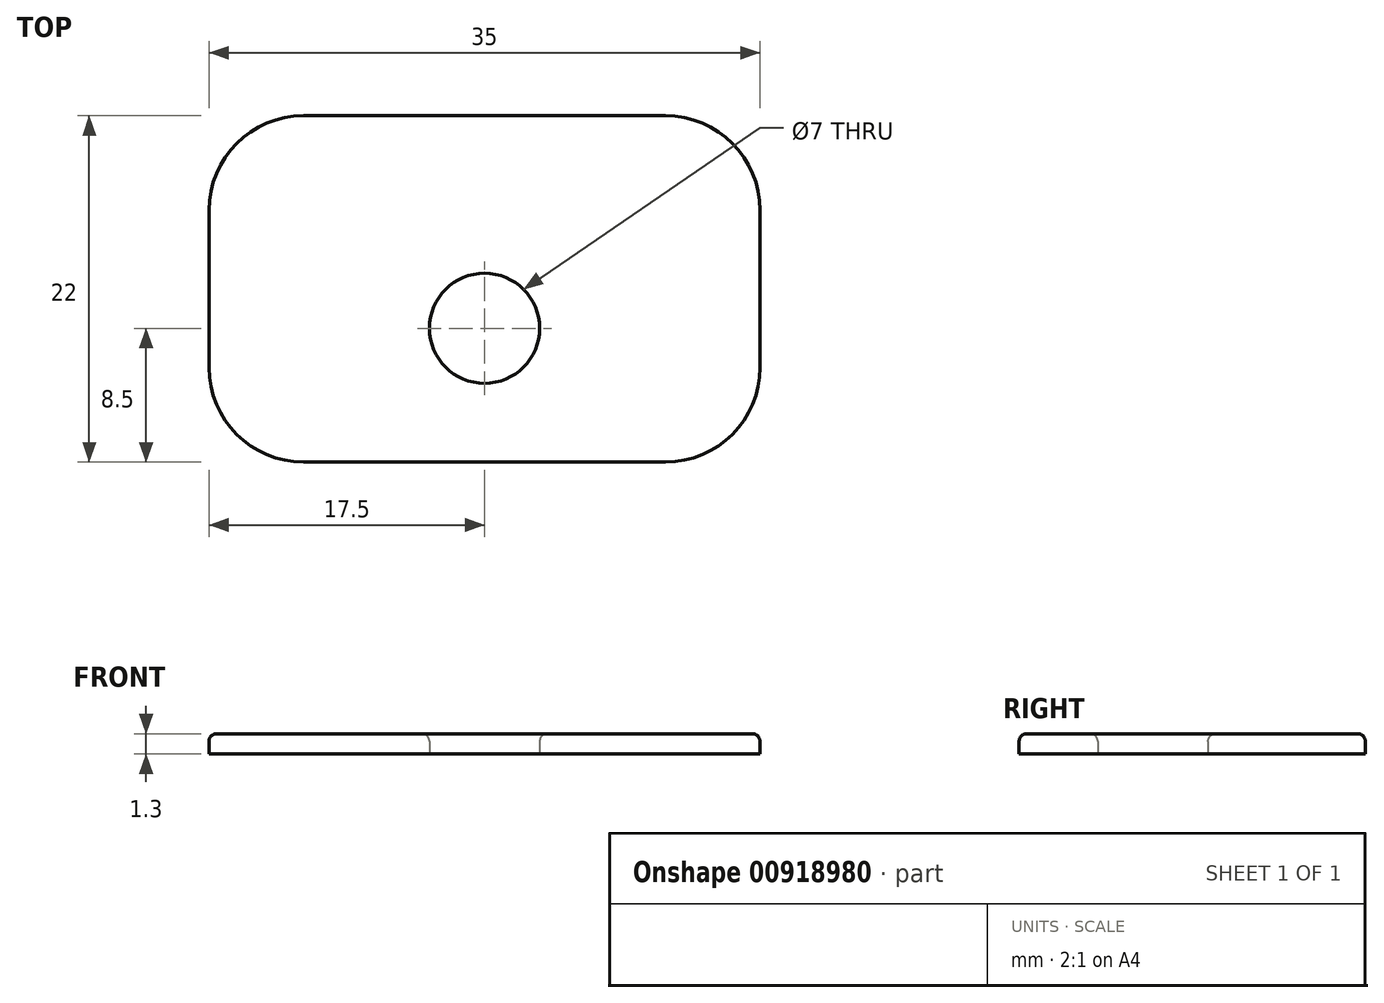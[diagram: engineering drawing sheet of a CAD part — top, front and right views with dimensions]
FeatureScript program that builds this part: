
annotation { "Feature Type Name" : "Feature", "Feature Type Description" : "" }
export const myFeature = defineFeature(function(context is Context, id is Id, definition is map)
    precondition{}
    {
        {
            var Q0;
            Q0=qCreatedBy(makeId("Top.planeOp"),FACE);
            var sketch = newSketch(context, id + "F0", { "sketchPlane" : qUnion([Q0])});
            skCircle(sketch, "E0", {"center": v(0, 0) * mm, "radius": 3.5 * mm});
            skLineSegment(sketch, "E1.bottom", {"start": v(-17.5, 13.5) * mm, "end": v(17.5, 13.5) * mm});
            skLineSegment(sketch, "E1.top", {"start": v(-17.5, -8.5) * mm, "end": v(17.5, -8.5) * mm});
            skLineSegment(sketch, "E1.left", {"start": v(-17.5, 13.5) * mm, "end": v(-17.5, -8.5) * mm});
            skLineSegment(sketch, "E1.right", {"start": v(17.5, 13.5) * mm, "end": v(17.5, -8.5) * mm});
            skPoint(sketch, "E2", {"position": v(0, -8.5) * mm});
            skSolve(sketch);
        }
        {
            var Q0;
            Q0 = qSketchRegion(id + "F0", true);
            extrude(context, id + "F1", {"entities" : qUnion([Q0]), "depth" : 1.3 * mm, "offsetDistance" : 25 * mm});
        }
        {
            var Q0;
            Q0=makeQuery(id+"F1.opExtrude","SWEPT_EDGE",EDGE,{"disambiguationData":[OSD([sQuery(id+"F0.wireOp",EDGE,"E1.bottom"),sQuery(id+"F0.wireOp",EDGE,"E1.right")])]});
            var Q1;
            Q1=makeQuery(id+"F1.opExtrude","SWEPT_EDGE",EDGE,{"disambiguationData":[OSD([sQuery(id+"F0.wireOp",EDGE,"E1.bottom"),sQuery(id+"F0.wireOp",EDGE,"E1.left")])]});
            var Q2;
            Q2=makeQuery(id+"F1.opExtrude","SWEPT_EDGE",EDGE,{"disambiguationData":[OSD([sQuery(id+"F0.wireOp",EDGE,"E1.top"),sQuery(id+"F0.wireOp",EDGE,"E1.left")])]});
            var Q3;
            Q3=makeQuery(id+"F1.opExtrude","SWEPT_EDGE",EDGE,{"disambiguationData":[OSD([sQuery(id+"F0.wireOp",EDGE,"E1.top"),sQuery(id+"F0.wireOp",EDGE,"E1.right")])]});
            fillet(context, id + "F2", {"entities" : qUnion([Q0, Q1, Q2, Q3]), "radius" : 6 * mm, "tangentPropagation" : true, "allowEdgeOverflow" : false});
        }
        {
            var Q0;
            Q0=makeQuery(id+"F1.opExtrude","CAP_FACE",FACE,{"disambiguationData":[OSD([sQuery(id+"F0.wireOp",EDGE,"E0"),sQuery(id+"F0.wireOp",EDGE,"E1.bottom"),sQuery(id+"F0.wireOp",EDGE,"E1.top"),sQuery(id+"F0.wireOp",EDGE,"E1.left"),sQuery(id+"F0.wireOp",EDGE,"E1.right")])],"isStart":false});
            fillet(context, id + "F3", {"entities" : qUnion([Q0]), "radius" : 0.5 * mm, "tangentPropagation" : true, "allowEdgeOverflow" : false});
        }
    });
